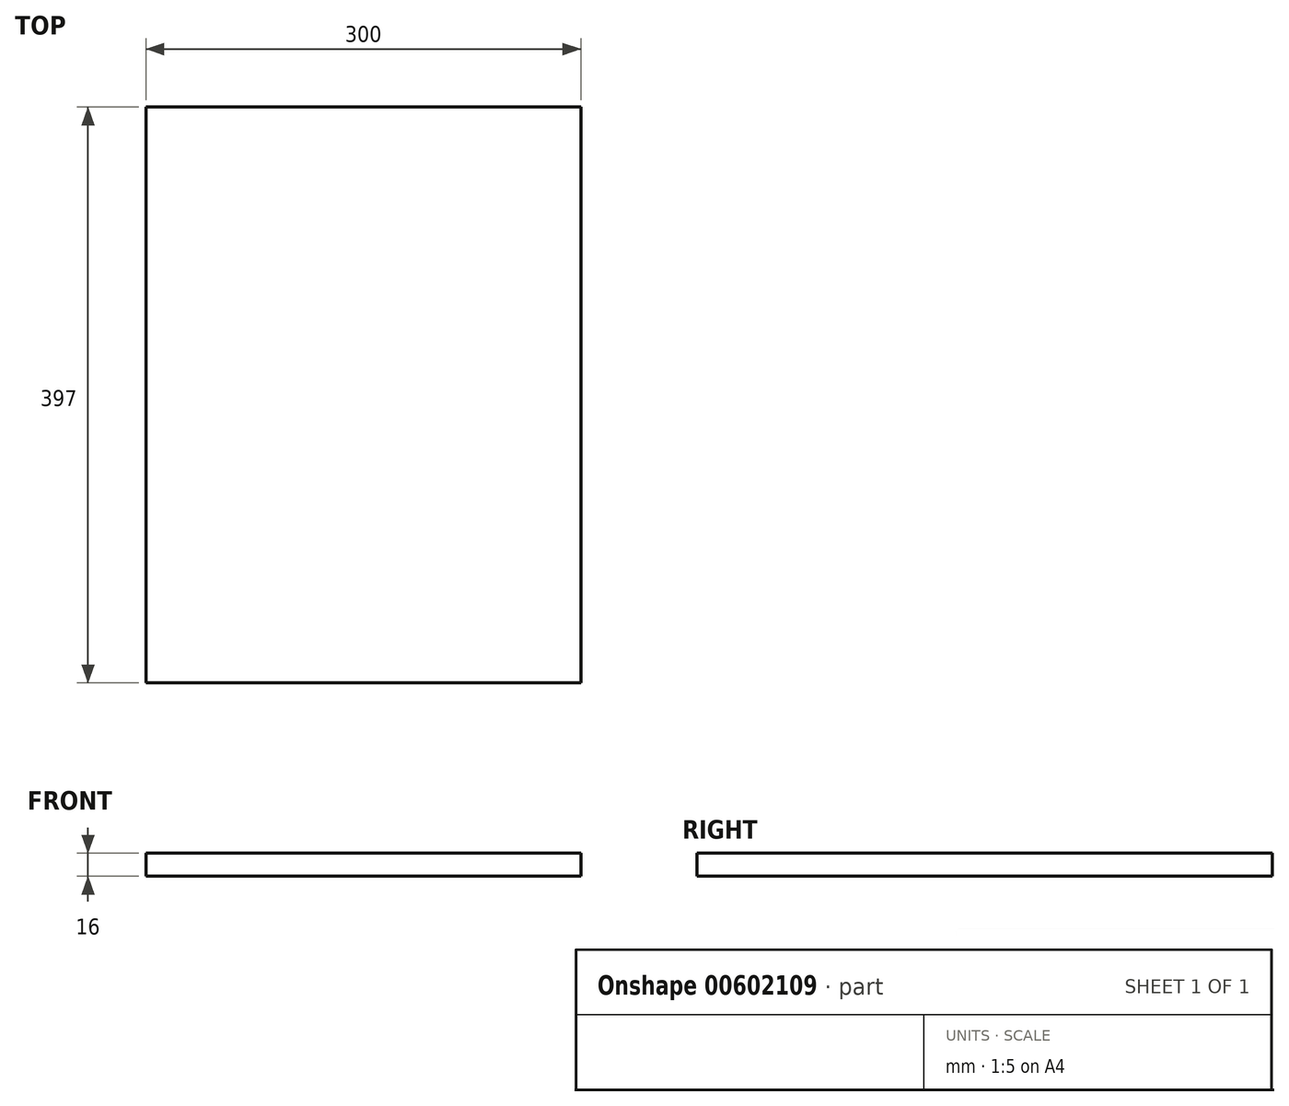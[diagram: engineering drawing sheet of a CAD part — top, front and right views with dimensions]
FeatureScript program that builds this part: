
annotation { "Feature Type Name" : "Feature", "Feature Type Description" : "" }
export const myFeature = defineFeature(function(context is Context, id is Id, definition is map)
    precondition{}
    {
        {
            var Q0;
            Q0=qCreatedBy(makeId("Top.planeOp"),FACE);
            var sketch = newSketch(context, id + "F0", { "sketchPlane" : qUnion([Q0])});
            skLineSegment(sketch, "E0.bottom", {"start": v(300, -397) * mm, "end": v(0, -397) * mm});
            skLineSegment(sketch, "E0.top", {"start": v(300, 0) * mm, "end": v(0, 0) * mm});
            skLineSegment(sketch, "E0.left", {"start": v(300, -397) * mm, "end": v(300, 0) * mm});
            skLineSegment(sketch, "E0.right", {"start": v(0, -397) * mm, "end": v(0, 0) * mm});
            skSolve(sketch);
        }
        {
            var Q0;
            Q0 = qSketchRegion(id + "F0", true);
            extrude(context, id + "F1", {"entities" : qUnion([Q0]), "depth" : 16 * mm, "offsetDistance" : 25 * mm});
        }
    });
